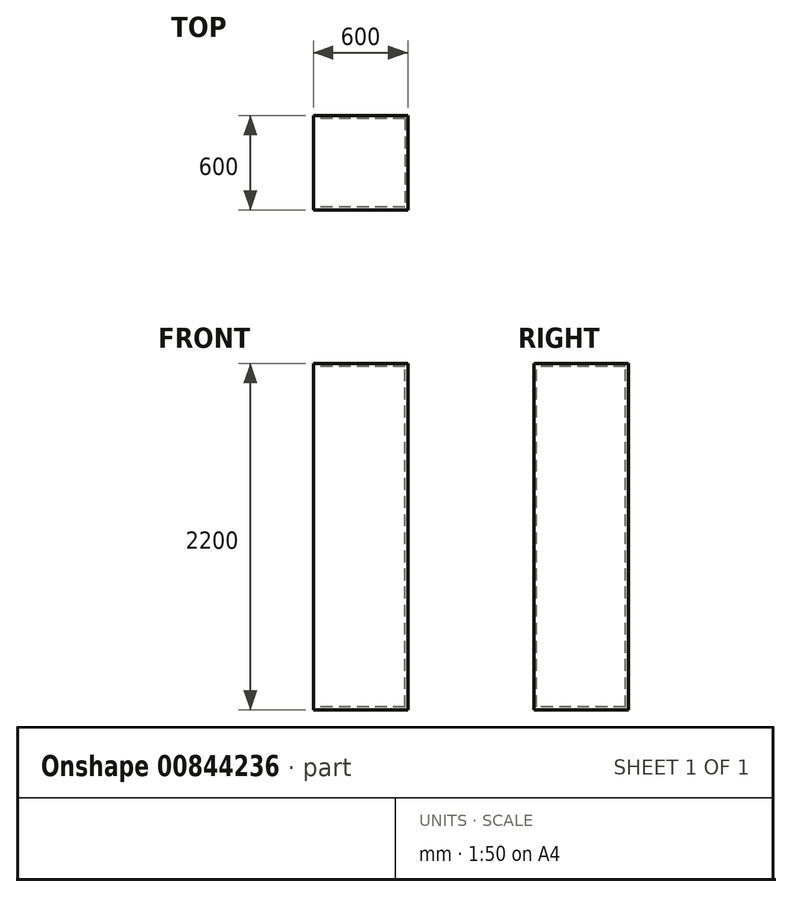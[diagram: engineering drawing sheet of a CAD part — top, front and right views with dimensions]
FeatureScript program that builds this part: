
annotation { "Feature Type Name" : "Feature", "Feature Type Description" : "" }
export const myFeature = defineFeature(function(context is Context, id is Id, definition is map)
    precondition{}
    {
        {
            var Q0;
            Q0=qCreatedBy(makeId("Right.planeOp"),FACE);
            var sketch = newSketch(context, id + "F0", { "sketchPlane" : qUnion([Q0])});
            skLineSegment(sketch, "E0.bottom", {"start": v(0, 0) * mm, "end": v(-40.86, 0) * mm});
            skLineSegment(sketch, "E0.top", {"start": v(0, 43.75) * mm, "end": v(-40.86, 43.75) * mm});
            skLineSegment(sketch, "E0.left", {"start": v(0, 0) * mm, "end": v(0, 43.75) * mm});
            skLineSegment(sketch, "E0.right", {"start": v(-40.86, 0) * mm, "end": v(-40.86, 43.75) * mm});
            skSolve(sketch);
        }
        {
            var Q0;
            Q0=makeQuery(id+"F0.imprint","IMPRINT",FACE,{"disambiguationData":[TD([[makeQuery(id+"F0.imprint","IMPRINT",EDGE,{"derivedFrom":sQuery(id+"F0.wireOp",EDGE,"E0.bottom")}),-1.0]])]});
            extrude(context, id + "F1", {"entities" : qUnion([Q0]), "depth" : 600 * mm, "offsetDistance" : 25 * mm});
        }
        {
            var Q0;
            Q0=makeQuery(id+"F1.opExtrude","SWEPT_FACE",FACE,{"disambiguationData":[OSD([sQuery(id+"F0.wireOp",EDGE,"E0.left")])]});
            extrude(context, id + "F2", {"entities" : qUnion([Q0]), "operationType" : NewBodyOperationType.ADD, "oppositeDirection" : true, "depth" : 600 * mm, "offsetDistance" : 25 * mm});
        }
        {
            var Q0;
            {var subQ0=sQuery(id+"F0.wireOp",EDGE,"E0.bottom");Q0=makeQuery(id+"F2.boolean.opBoolean","MERGE",FACE,{"derivedFrom":[makeQuery(id+"F1.opExtrude","SWEPT_FACE",FACE,{"disambiguationData":[OSD([subQ0])]}),makeQuery(id+"F2.opExtrude","SWEPT_FACE",FACE,{"disambiguationData":[OSD([subQ0,sQuery(id+"F0.wireOp",EDGE,"E0.left")])]})]});}
            extrude(context, id + "F3", {"entities" : qUnion([Q0]), "operationType" : NewBodyOperationType.ADD, "oppositeDirection" : true, "depth" : 2200 * mm, "offsetDistance" : 25 * mm});
        }
        {
            var Q0;
            {var subQ0=sQuery(id+"F0.wireOp",EDGE,"E0.left");var subQ1=sQuery(id+"F0.wireOp",EDGE,"E0.bottom");Q0=makeQuery(id+"F3.boolean.opBoolean","MERGE",FACE,{"derivedFrom":[makeQuery(id+"F2.boolean.opBoolean","MERGE",FACE,{"derivedFrom":[makeQuery(id+"F1.opExtrude","CAP_FACE",FACE,{"disambiguationData":[OSD([subQ1,sQuery(id+"F0.wireOp",EDGE,"E0.top"),subQ0,sQuery(id+"F0.wireOp",EDGE,"E0.right")])],"isStart":true}),makeQuery(id+"F2.opExtrude","SWEPT_FACE",FACE,{"disambiguationData":[OSD([subQ0]),TDD([makeQuery(id+"F1.opExtrude","CAP_EDGE",EDGE,{"disambiguationData":[OSD([subQ0])],"isStart":true})])]})]}),makeQuery(id+"F3.opExtrude","SWEPT_FACE",FACE,{"disambiguationData":[OSD([subQ1,subQ0]),TDD([makeQuery(id+"F2.boolean.opBoolean","MERGE",EDGE,{"derivedFrom":[makeQuery(id+"F1.opExtrude","CAP_EDGE",EDGE,{"disambiguationData":[OSD([subQ1])],"isStart":true}),makeQuery(id+"F2.opExtrude","SWEPT_EDGE",EDGE,{"disambiguationData":[OSD([subQ1,subQ0]),TDD([makeQuery(id+"F1.opExtrude","CAP_VERTEX",VERTEX,{"disambiguationData":[OSD([subQ1,subQ0])],"isStart":true})])]})]})])]})]});}
            shell(context, id + "F4", {"entities" : qUnion([Q0]), "thickness" : 18 * mm});
        }
    });
